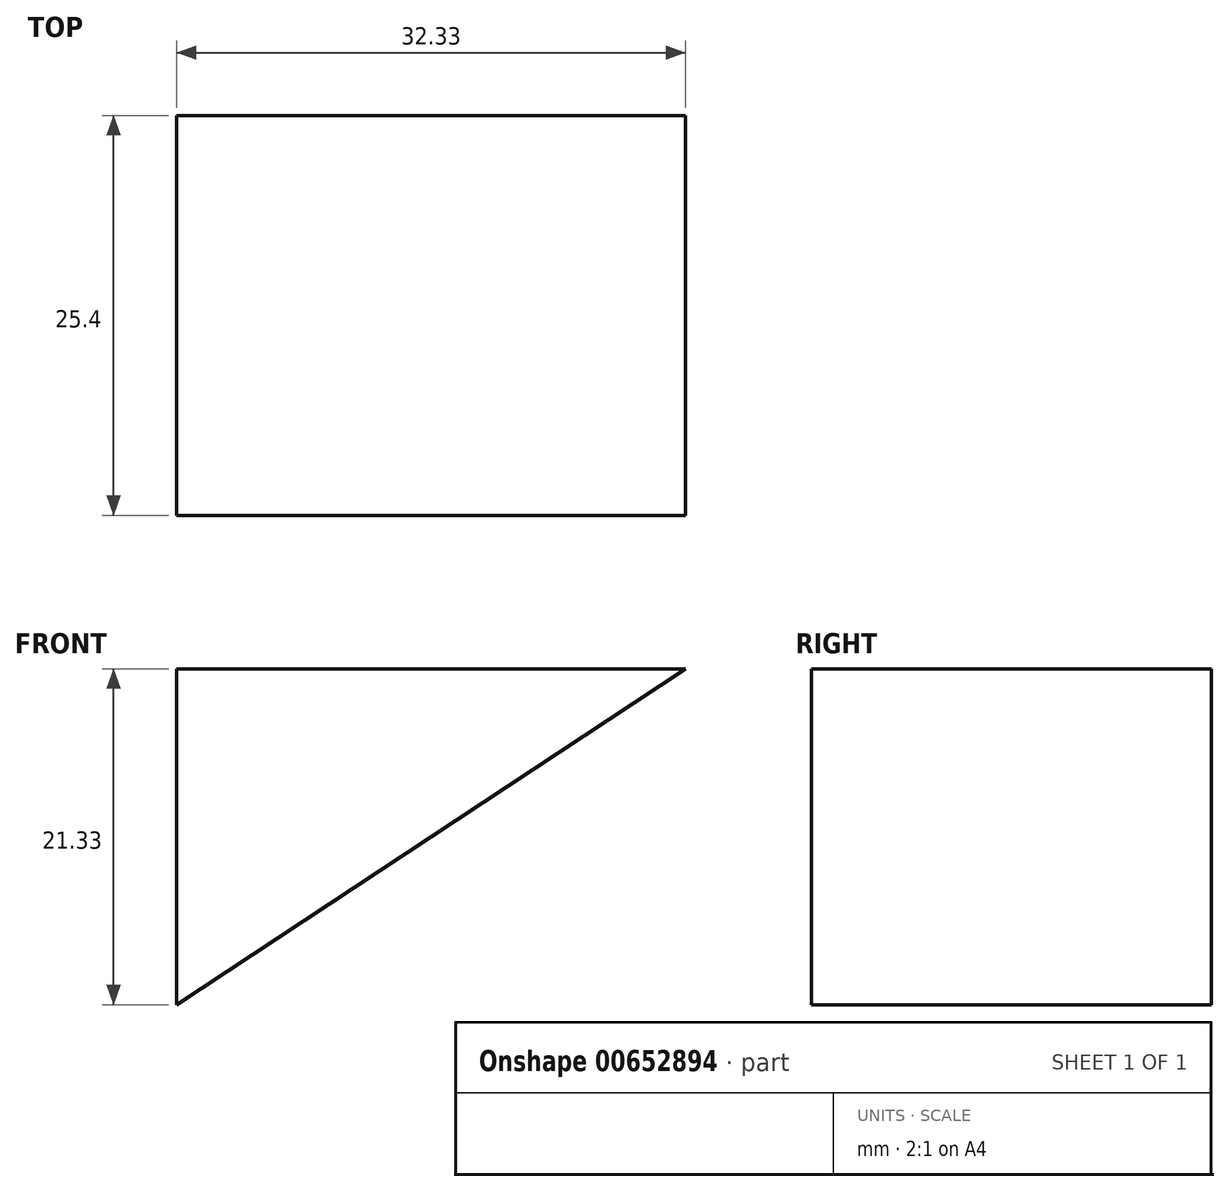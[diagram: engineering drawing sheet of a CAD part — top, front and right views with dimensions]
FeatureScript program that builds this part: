
annotation { "Feature Type Name" : "Feature", "Feature Type Description" : "" }
export const myFeature = defineFeature(function(context is Context, id is Id, definition is map)
    precondition{}
    {
        {
            var Q0;
            Q0=qCreatedBy(makeId("Front.planeOp"),FACE);
            var sketch = newSketch(context, id + "F0", { "sketchPlane" : qUnion([Q0])});
            skLineSegment(sketch, "E0", {"start": v(-55.84, 21.33) * mm, "end": v(0, 21.33) * mm});
            skLineSegment(sketch, "E1", {"start": v(0, 21.33) * mm, "end": v(-32.33, 0) * mm});
            skLineSegment(sketch, "E2", {"start": v(-32.33, 0) * mm, "end": v(-32.33, 21.33) * mm});
            skSolve(sketch);
        }
        {
            var Q0;
            {var subQ0=sQuery(id+"F0.wireOp",EDGE,"E1");Q0=makeQuery(id+"F0.imprint","IMPRINT",FACE,{"disambiguationData":[TD([[makeQuery(id+"F0.imprint","IMPRINT",EDGE,{"derivedFrom":subQ0}),-1.0]])]});}
            extrude(context, id + "F1", {"entities" : qUnion([Q0]), "depth" : 25.4 * mm, "offsetDistance" : 25.4 * mm});
        }
    });
